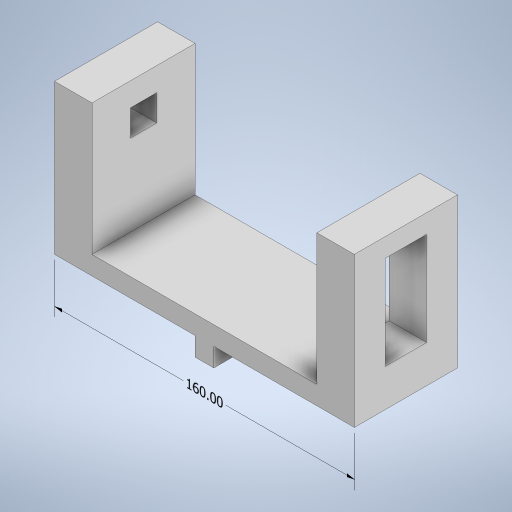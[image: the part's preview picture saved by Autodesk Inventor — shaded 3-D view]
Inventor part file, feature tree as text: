
AUTODESK INVENTOR PART (.ipt)
format: ipt  version: 2023 (Build 270158000, 158)  size: 271,360 bytes
history: native  units: mm
features: extrude x5, sketch x5, other x3
ambient origin geometry x8: Origin, YZ Plane, XZ Plane, XY Plane, X Axis, Y Axis, Z Axis, Center Point
bodies: Body1 (feature_tree)
feature tree (13):
  other  "Sólido1"
  other  "Anotaciones"
  extrude  "Extrusión1"  Depth=10.0mm
  extrude  "Extrusión2"  Depth=20.0mm
  extrude  "Extrusión3"  Depth=70.0mm TaperAngle=0.0deg
  extrude  "Extrusión4"  Depth=14.0mm
  extrude  "Extrusión5"  Depth=12.5mm
  sketch  "Boceto1"  dims[d0=160.0mm d1=10.0mm]
  sketch  "Boceto2"  dims[d2=55.0mm d3=0.0mm d4=20.0mm]
  sketch  "Boceto3"  dims[d5=20.0mm d6=70.0mm d7=0.0mm]
  sketch  "Boceto4"  dims[d10=14.0mm d11=14.0mm]
  sketch  "Boceto5"  dims[d12=20.5mm d13=12.5mm d14=70.0mm d15=0.0mm d17=10.0mm d18=10.0mm d19=0.0mm d24=30.0mm d25=0.0mm d26=50.0mm d27=22.0mm d28=16.5mm d29=10.0mm d30=30.0mm d31=3.205196mm d32=3.393248mm d33=160.0mm]
  other  "Cota lineal 1"
